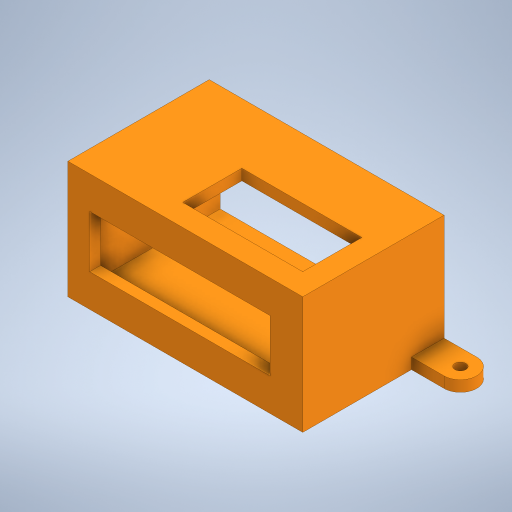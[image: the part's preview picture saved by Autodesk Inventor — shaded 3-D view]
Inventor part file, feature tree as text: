
AUTODESK INVENTOR PART (.ipt)
format: ipt  version: 2023 (Build 270158000, 158)  size: 279,552 bytes
history: native  units: mm
features: extrude x4, sketch x4
ambient origin geometry x8: Origin, YZ Plane, XZ Plane, XY Plane, X Axis, Y Axis, Z Axis, Center Point
bodies: Solid1 (feature_tree)
feature tree (8):
  extrude  "Extrusion1"  Depth=44.0mm
  extrude  "Extrusion2"  Depth=5.0mm
  extrude  "Extrusion4"  Depth=5.0mm
  extrude  "Extrusion5"  Depth=5.0mm TaperAngle=0.0deg
  sketch  "Sketch1"  dims[d0=98.0mm d1=44.0mm]
  sketch  "Sketch2"  dims[d2=5.0mm d3=5.0mm]
  sketch  "Sketch4"  dims[d4=5.0mm d5=5.0mm]
  sketch  "Sketch5"  dims[d6=60.0mm d7=0.0mm d8=5.0mm d9=0.0mm d10=10.0mm d11=15.0mm d12=15.0mm d13=15.0mm d19=27.2mm d20=55.2mm d21=10.0mm d22=10.0mm d23=10.0mm d24=0.0mm d25=15.0mm d26=5.0mm d27=15.0mm d28=5.0mm d29=0.0mm]
